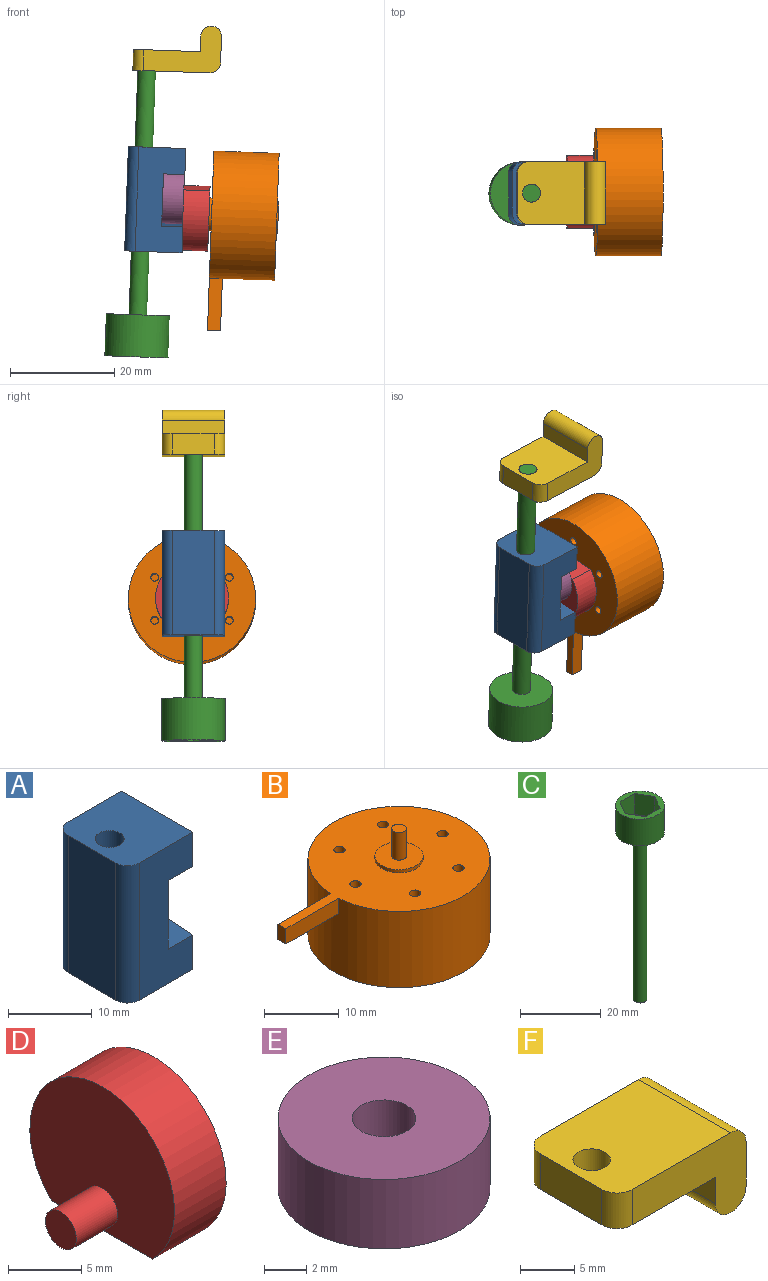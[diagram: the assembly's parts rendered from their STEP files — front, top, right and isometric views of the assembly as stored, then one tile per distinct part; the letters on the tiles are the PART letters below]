
ASSEMBLY  parts=6 mates=5
PART A: 13 faces, bbox 11x12x20 mm
  f0: plane 12x6mm, normal (1,0,0), area 66mm2, adj f1,f5,f6,f7
  f1: plane 20x9mm, normal (0,-1,0), area 139mm2, adj f0,f2,f3,f5,f7,f8,f9,f12
  f2: plane 12x5mm, normal (1,0,0), area 54mm2, adj f1,f3,f6,f8
  f3: plane 12x11mm, normal (0,0,1), area 120.9mm2, adj f1,f2,f4,f6,f10,f11,f12
  f4: plane 20x8mm, normal (-1,0,0), area 160mm2, adj f3,f5,f11,f12
  f5: plane 12x11mm, normal (0,0,-1), area 120.9mm2, adj f0,f1,f4,f6,f10,f11,f12
  f6: plane 20x9mm, normal (0,1,0), area 139mm2, adj f0,f2,f3,f5,f7,f8,f9,f11
  f7: plane 12x4.1mm, normal (0,-0.08,1), area 49.4mm2, adj f0,f1,f6,f9
  f8: plane 12x4.1mm, normal (0,0.08,-1), area 49.4mm2, adj f1,f2,f6,f9
  f9: plane 12x11mm, normal (1,0,0), area 120mm2, adj f1,f6,f7,f8
  f10: cylinder r=1.73mm len=20mm, axis (0,0,1), area 217mm2, adj f3,f5
  f11: cylinder r=2mm len=20mm, axis (0,0,-1), area 62.8mm2, adj f3,f4,f5,f6
  f12: cylinder r=2mm len=20mm, axis (0,0,1), area 62.8mm2, adj f1,f3,f4,f5
PART B: 25 faces, bbox 34.4x24.4x17.8 mm
  f0: cylinder r=12.2mm len=24.4mm, axis (0,0,-1), area 954.4mm2, adj f1,f2,f21,f22,f24
  f1: plane 34.38x24.4mm, normal (0,0,1), area 439.3mm2, adj f0,f3,f7,f9,f11,f13,f15,f17
  f2: plane 24.4x24.4mm, normal (0,0,-1), area 438.4mm2, adj f0,f19
  f3: cylinder r=3.23mm len=6.45mm, axis (0,0,-1), area 10.1mm2, adj f1,f4
  f4: plane 6.45x6.45mm, normal (0,0,1), area 29.5mm2, adj f3,f5
  f5: cylinder r=1mm len=4.5mm, axis (0,0,-1), area 28.3mm2, adj f4,f6
  f6: plane 2x2mm, normal (0,0,1), area 3.1mm2, adj f5
  f7: cylinder r=0.75mm len=5mm, axis (0,0,1), area 23.6mm2, adj f1,f8
  f8: plane 1.5x1.5mm, normal (0,0,1), area 1.8mm2, adj f7
  f9: cylinder r=0.75mm len=5mm, axis (0,0,1), area 23.6mm2, adj f1,f10
  f10: plane 1.5x1.5mm, normal (0,0,1), area 1.8mm2, adj f9
  f11: cylinder r=0.75mm len=5mm, axis (0,0,1), area 23.6mm2, adj f1,f12
  f12: plane 1.5x1.5mm, normal (0,0,1), area 1.8mm2, adj f11
  f13: cylinder r=0.75mm len=5mm, axis (0,0,1), area 23.6mm2, adj f1,f14
  f14: plane 1.5x1.5mm, normal (0,0,1), area 1.8mm2, adj f13
  f15: cylinder r=0.75mm len=5mm, axis (0,0,1), area 23.6mm2, adj f1,f16
  f16: plane 1.5x1.5mm, normal (0,0,1), area 1.8mm2, adj f15
  f17: cylinder r=0.75mm len=5mm, axis (0,0,1), area 23.6mm2, adj f1,f18
  f18: plane 1.5x1.5mm, normal (0,0,1), area 1.8mm2, adj f17
  f19: cylinder r=3.05mm len=6.1mm, axis (0,0,1), area 4.8mm2, adj f2,f20
  f20: plane 6.1x6.1mm, normal (0,0,-1), area 29.2mm2, adj f19
  f21: plane 10x2.5mm, normal (0,-1,0), area 25mm2, adj f0,f1,f23,f24
  f22: plane 10x2.5mm, normal (0,1,0), area 25mm2, adj f0,f1,f23,f24
  f23: plane 2.5x1.5mm, normal (-1,0,0), area 3.8mm2, adj f1,f21,f22,f24
  f24: plane 10x1.5mm, normal (0,0,-1), area 15mm2, adj f0,f21,f22,f23
PART C: 12 faces, bbox 12.1x12.1x58.9 mm
  f0: cylinder r=1.73mm len=50.8mm, axis (0,0,-1), area 551.3mm2, adj f1,f4
  f1: plane 3.45x3.45mm, normal (0,0,-1), area 9.4mm2, adj f0
  f2: cylinder r=6.07mm len=12.14mm, axis (0,0,-1), area 307.1mm2, adj f3,f4
  f3: plane 12.14x12.14mm, normal (0,0,1), area 46.4mm2, adj f2,f5,f6,f7,f8,f9,f10
  f4: plane 12.14x12.14mm, normal (0,0,-1), area 106.4mm2, adj f0,f2
  f5: plane 6.35x5.17mm, normal (0,1,0), area 32.8mm2, adj f3,f6,f10,f11
  f6: plane 6.35x4.47mm, normal (-0.87,0.5,0), area 32.8mm2, adj f3,f5,f7,f11
  f7: plane 6.35x4.47mm, normal (-0.87,-0.5,0), area 32.8mm2, adj f3,f6,f8,f11
  f8: plane 6.35x5.17mm, normal (0,-1,0), area 32.8mm2, adj f3,f7,f9,f11
  f9: plane 6.35x4.47mm, normal (0.87,-0.5,0), area 32.8mm2, adj f3,f8,f10,f11
  f10: plane 6.35x4.47mm, normal (0.87,0.5,0), area 32.8mm2, adj f3,f5,f9,f11
  f11: plane 10.33x8.95mm, normal (0,0,1), area 69.3mm2, adj f5,f6,f7,f8,f9,f10
PART D: 8 faces, bbox 9x14x12 mm
  f0: plane 9.8x5mm, normal (0,0,-1), area 49mm2, adj f1,f2,f3
  f1: cylinder r=7mm len=14mm, axis (-1,0,0), area 165.6mm2, adj f0,f2,f3
  f2: plane 14x12mm, normal (1,0,0), area 137.3mm2, adj f0,f1,f4
  f3: plane 14x12mm, normal (-1,0,0), area 133.4mm2, adj f0,f1,f6
  f4: cylinder r=1mm len=4.5mm, axis (1,0,0), area 28.3mm2, adj f2,f5
  f5: plane 2x2mm, normal (1,0,0), area 3.1mm2, adj f4
  f6: cylinder r=1.5mm len=4mm, axis (1,0,0), area 37.7mm2, adj f3,f7
  f7: plane 3x3mm, normal (-1,0,0), area 7.1mm2, adj f6
PART E: 4 faces, bbox 10x10x4 mm
  f0: cylinder r=5mm len=10mm, axis (0,0,-1), area 125.7mm2, adj f1,f2
  f1: plane 10x10mm, normal (0,0,1), area 71.5mm2, adj f0,f3
  f2: plane 10x10mm, normal (0,0,-1), area 71.5mm2, adj f0,f3
  f3: cylinder r=1.5mm len=4mm, axis (0,0,1), area 37.7mm2, adj f1,f2
PART F: 12 faces, bbox 16.8x12x9 mm
  f0: plane 12x3mm, normal (-1,0,0), area 36mm2, adj f4,f5,f6,f7
  f1: plane 12x5mm, normal (1,0,0), area 60mm2, adj f5,f6,f7,f8
  f2: plane 14.75x12mm, normal (0,0,1), area 165.9mm2, adj f3,f5,f6,f8,f9,f10,f11
  f3: plane 8x4mm, normal (-1,0,0), area 32mm2, adj f2,f4,f9,f10
  f4: plane 12.75x12mm, normal (0,0,-1), area 141.9mm2, adj f0,f3,f5,f6,f9,f10,f11
  f5: plane 14.75x9mm, normal (0,1,0), area 76.4mm2, adj f0,f1,f2,f4,f7,f8,f10
  f6: plane 14.75x9mm, normal (0,-1,0), area 76.4mm2, adj f0,f1,f2,f4,f7,f8,f9
  f7: cylinder r=2mm len=12mm, axis (0,-1,0), area 75.4mm2, adj f0,f1,f5,f6
  f8: cylinder r=2mm len=12mm, axis (0,-1,0), area 37.7mm2, adj f1,f2,f5,f6
  f9: cylinder r=2mm len=4mm, axis (0,0,-1), area 12.6mm2, adj f2,f3,f4,f6
  f10: cylinder r=2mm len=4mm, axis (0,0,1), area 12.6mm2, adj f2,f3,f4,f5
  f11: cylinder r=1.73mm len=4mm, axis (0,0,1), area 43.4mm2, adj f2,f4
PLACE A rot(axis=(0,1,0),2.1deg) t=(-75.38,38.61,-58.62)mm
PLACE B rot(axis=(0,-1,0),87.9deg) t=(-66.86,32.87,-41.4)mm
PLACE C rot(axis=(0,-1,0),177.9deg) t=(-91.62,32.61,-9.37)mm
PLACE D rot(axis=(-1,0,0.02),175deg) t=(-84.85,32.87,-40.75)mm
PLACE E rot(axis=(0,-1,0),87.9deg) t=(-84.74,32.61,-37.77)mm
PLACE F rot(axis=(-1,0,0.02),180deg) t=(-67.03,38.61,4.76)mm
MATE revolute D.f4 <-> B.f5  axis (1,0,-0.04) through (-84.35,32.87,-40.77)mm
MATE revolute D.f6 <-> A.f9  axis (-1,0,0.04) through (-88.74,32.61,-37.62)mm
MATE revolute D.f6 <-> E.f3  axis (-1,0,0.04) through (-88.74,32.61,-37.62)mm
MATE fastened C.f0 <-> F.f11  axis (0.04,0,1) through (-91.62,32.61,-9.37)mm
MATE slider C.f0 <-> A.f10  axis (0.04,0,1) through (-92.54,32.61,-34.75)mm
